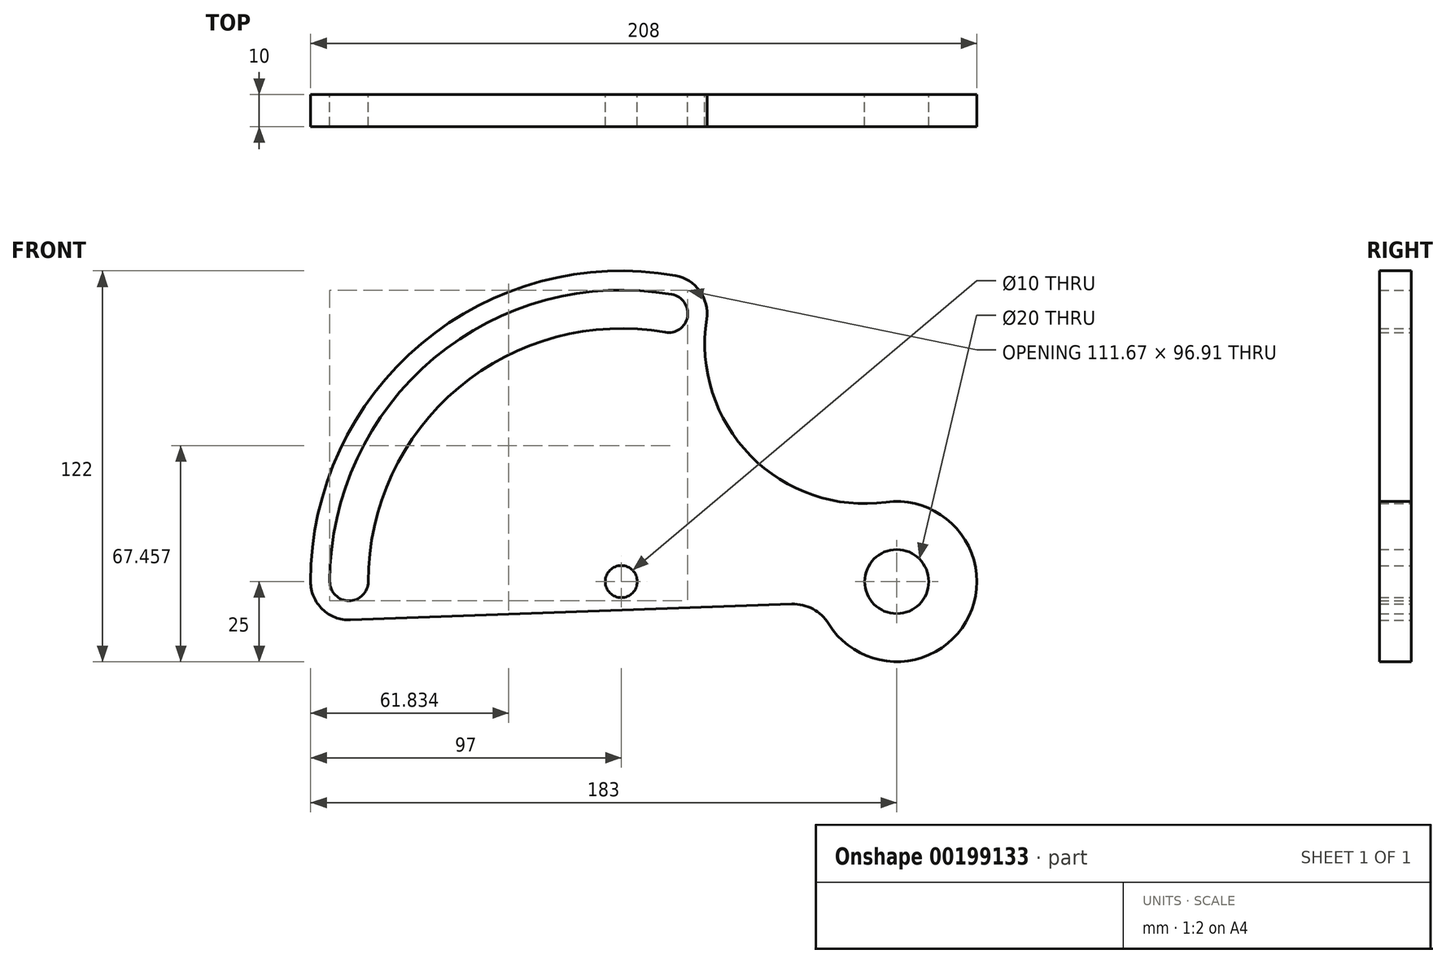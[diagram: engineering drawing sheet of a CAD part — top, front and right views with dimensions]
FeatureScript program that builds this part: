
annotation { "Feature Type Name" : "Feature", "Feature Type Description" : "" }
export const myFeature = defineFeature(function(context is Context, id is Id, definition is map)
    precondition{}
    {
        {
            var Q0;
            Q0=qCreatedBy(makeId("Front.planeOp"),FACE);
            var sketch = newSketch(context, id + "F0", { "sketchPlane" : qUnion([Q0])});
            skCircle(sketch, "E0", {"center": v(0, 0) * mm, "radius": 5 * mm});
            skLineSegment(sketch, "E1", {"start": v(0, 0) * mm, "end": v(14.76, 83.7) * mm, "construction": true});
            skArc(sketch, "E2", {"start": v(14.76, 83.7) * mm, "mid": v(-54.64, 65.11) * mm, "end": v(-85, 0) * mm, "construction": true});
            skArc(sketch, "E3", {"start": v(-79, 0) * mm, "mid": v(-85, -6) * mm, "end": v(-91, 0) * mm});
            skArc(sketch, "E4", {"start": v(13.72, 77.8) * mm, "mid": v(20.67, 82.67) * mm, "end": v(15.8, 89.62) * mm});
            skArc(sketch, "E5", {"start": v(13.72, 77.8) * mm, "mid": v(-50.78, 60.52) * mm, "end": v(-79, 0) * mm});
            skArc(sketch, "E6", {"start": v(15.8, 89.62) * mm, "mid": v(-58.5, 69.71) * mm, "end": v(-91, 0) * mm});
            skArc(sketch, "E7", {"start": v(16.84, 95.53) * mm, "mid": v(24.51, 90.7) * mm, "end": v(26.62, 81.9) * mm});
            skArc(sketch, "E8", {"start": v(-97, 0) * mm, "mid": v(-93.33, -8.64) * mm, "end": v(-84.57, -12) * mm});
            skArc(sketch, "E9", {"start": v(-97, 0) * mm, "mid": v(-62.35, 74.3) * mm, "end": v(16.84, 95.53) * mm});
            skArc(sketch, "E10", {"start": v(26.62, 81.9) * mm, "mid": v(40.36, 39.31) * mm, "end": v(82.68, 24.78) * mm});
            skCircle(sketch, "E11", {"center": v(86, 0) * mm, "radius": 10 * mm});
            skArc(sketch, "E12", {"start": v(82.68, 24.78) * mm, "mid": v(108.6, -10.69) * mm, "end": v(64.74, -13.16) * mm});
            skLineSegment(sketch, "E13", {"start": v(-84.57, -12) * mm, "end": v(53.22, -7) * mm});
            skArc(sketch, "E14", {"start": v(64.74, -13.16) * mm, "mid": v(59.8, -8.53) * mm, "end": v(53.22, -7) * mm});
            skSolve(sketch);
        }
        {
            var Q0;
            Q0 = qSketchRegion(id + "F0", true);
            extrude(context, id + "F1", {"entities" : qUnion([Q0]), "depth" : 10 * mm});
        }
    });
